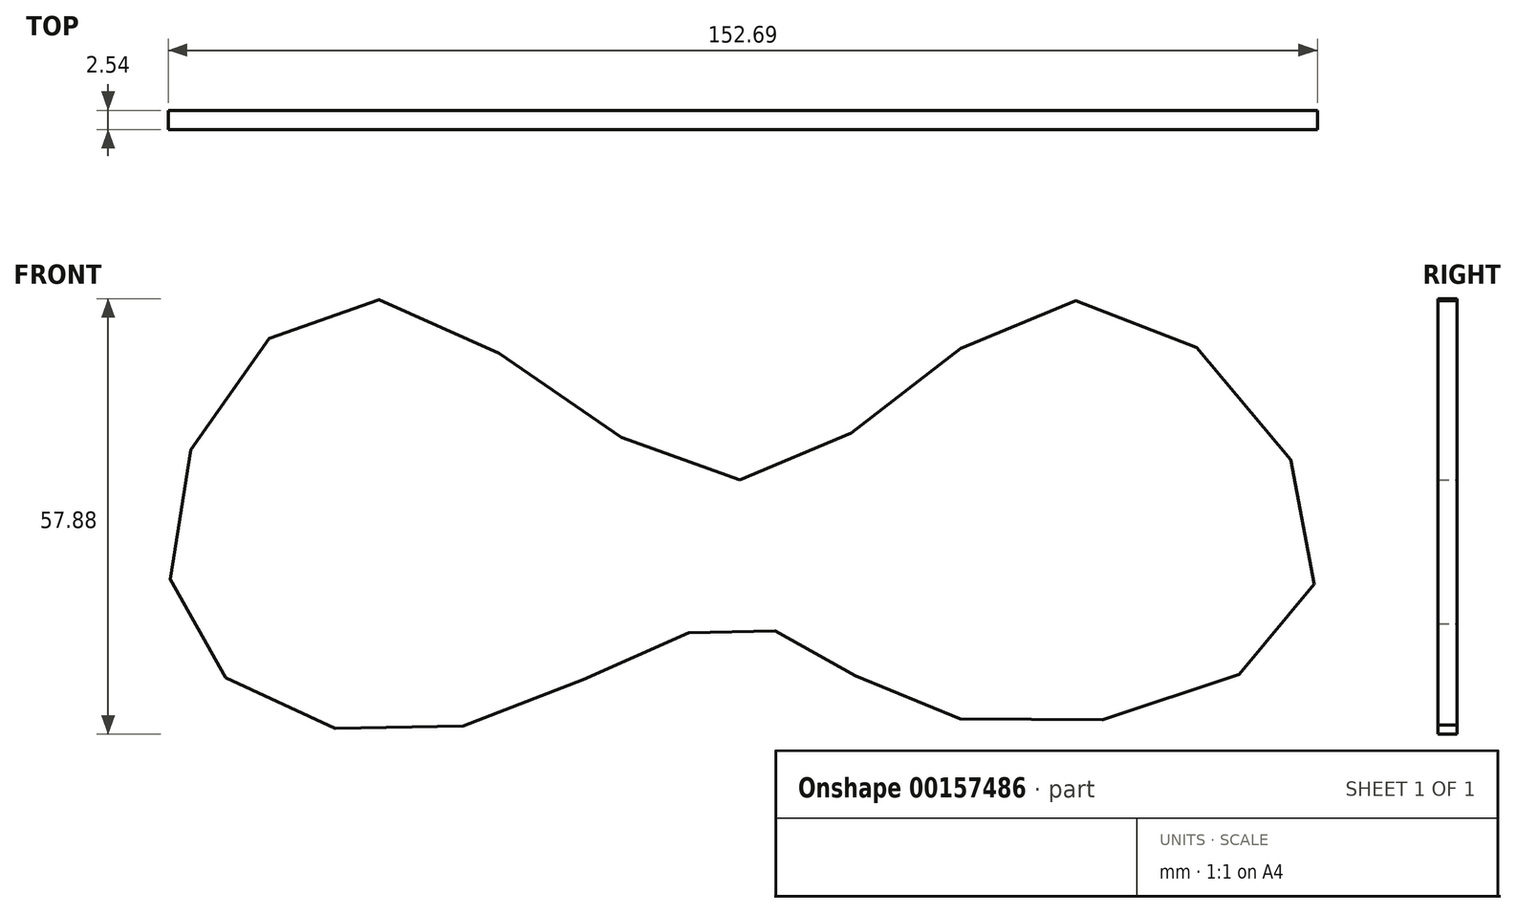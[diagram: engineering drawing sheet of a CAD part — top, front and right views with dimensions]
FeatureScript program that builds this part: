
annotation { "Feature Type Name" : "Feature", "Feature Type Description" : "" }
export const myFeature = defineFeature(function(context is Context, id is Id, definition is map)
    precondition{}
    {
        {
            var Q0;
            Q0=qCreatedBy(makeId("Front.planeOp"),FACE);
            var sketch = newSketch(context, id + "F0", { "sketchPlane" : qUnion([Q0])});
            skFitSpline(sketch, "E0", {"points": [v(0, 14.43) * mm, v(-51.03, 38.45) * mm, v(-75.5, 0) * mm, v(-40.87, -19.05) * mm, v(0, -4.73) * mm, v(27.7, -16.97) * mm, v(76.2, 0) * mm, v(45.49, 38.22) * mm, v(0, 14.43) * mm]});
            skSolve(sketch);
        }
        {
            var Q0;
            Q0=makeQuery(id+"F0.imprint","IMPRINT",FACE,{"disambiguationData":[TD([[makeQuery(id+"F0.imprint","IMPRINT",EDGE,{"derivedFrom":sQuery(id+"F0.wireOp",EDGE,"E0")}),1.0]])]});
            extrude(context, id + "F1", {"entities" : qUnion([Q0]), "depth" : 2.54 * mm});
        }
    });
